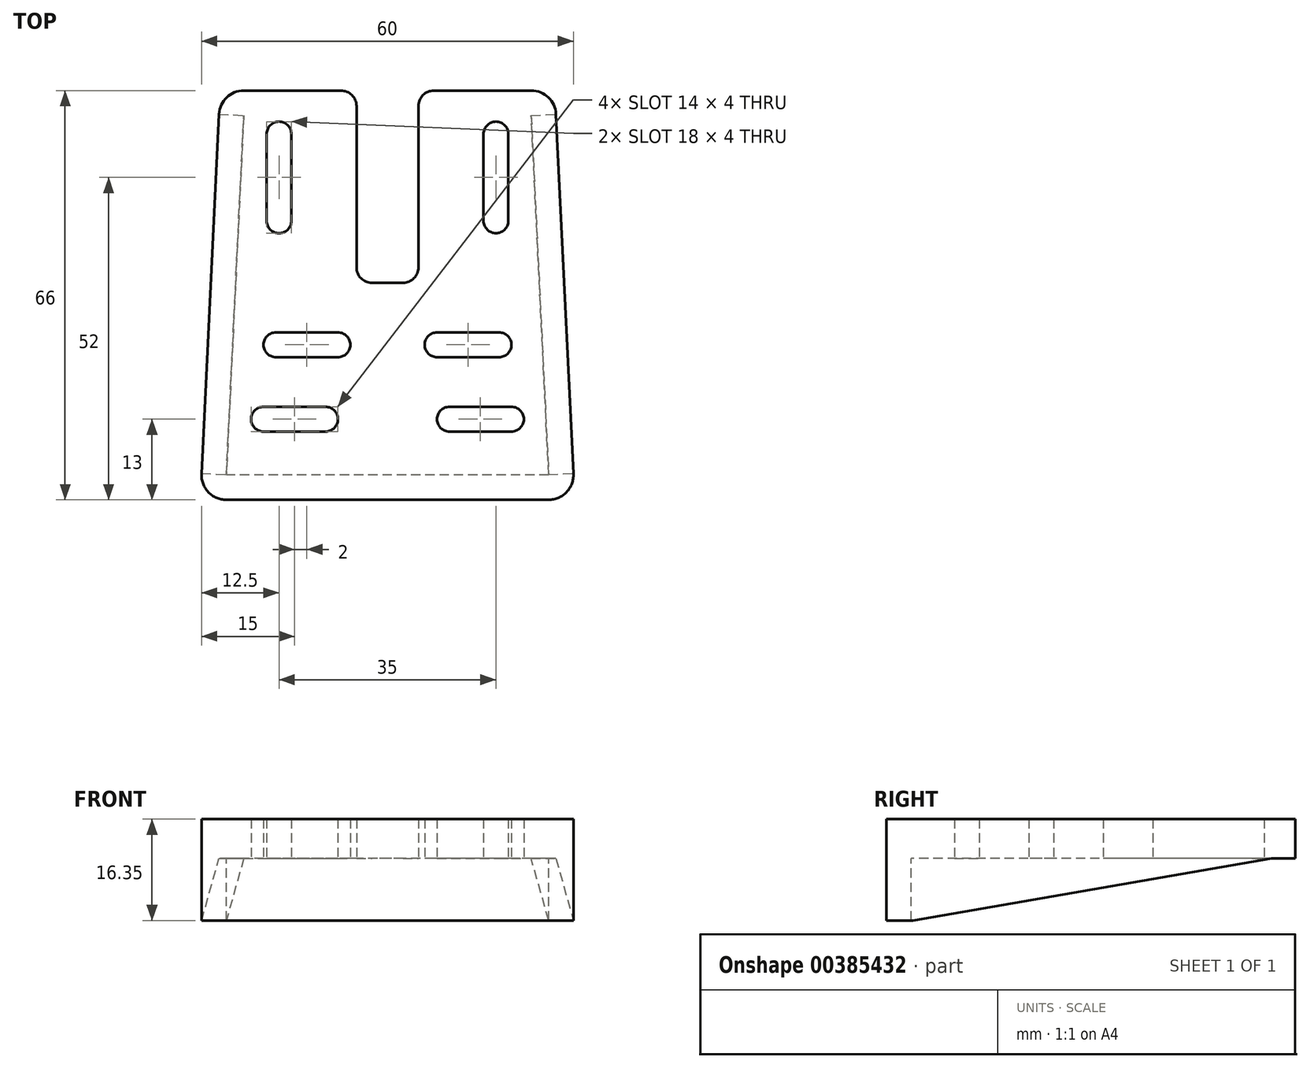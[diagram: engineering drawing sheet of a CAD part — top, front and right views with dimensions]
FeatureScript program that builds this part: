
annotation { "Feature Type Name" : "Feature", "Feature Type Description" : "" }
export const myFeature = defineFeature(function(context is Context, id is Id, definition is map)
    precondition{}
    {
        {
            var Q0;
            Q0=qCreatedBy(makeId("Top.planeOp"),FACE);
            var sketch = newSketch(context, id + "F0", { "sketchPlane" : qUnion([Q0])});
            skLineSegment(sketch, "E0", {"start": v(0, 0) * mm, "end": v(26, 0) * mm});
            skLineSegment(sketch, "E1", {"start": v(23.19, 66) * mm, "end": v(7.5, 66) * mm});
            skLineSegment(sketch, "E2", {"start": v(5, 63.5) * mm, "end": v(5, 37.5) * mm});
            skLineSegment(sketch, "E3", {"start": v(2.5, 35) * mm, "end": v(0, 35) * mm});
            skLineSegment(sketch, "E4.bottom", {"start": v(21, 61) * mm, "end": v(21, 61) * mm});
            skLineSegment(sketch, "E4.top", {"start": v(17, 35) * mm, "end": v(17, 35) * mm});
            skPoint(sketch, "E5.visualSharp", {"position": v(5, 35) * mm});
            skArc(sketch, "E5.filletArc", {"start": v(2.5, 35) * mm, "mid": v(4.27, 35.73) * mm, "end": v(5, 37.5) * mm});
            skPoint(sketch, "E6.visualSharp", {"position": v(5, 66) * mm});
            skArc(sketch, "E6.filletArc", {"start": v(7.5, 66) * mm, "mid": v(5.73, 65.27) * mm, "end": v(5, 63.5) * mm});
            skArc(sketch, "E7.filletArc", {"start": v(26, 0) * mm, "mid": v(28.9, 1.24) * mm, "end": v(30, 4.2) * mm});
            skLineSegment(sketch, "E8.MirrorCS", {"start": v(-21, 61) * mm, "end": v(-21, 61) * mm});
            skLineSegment(sketch, "E9.MirrorCS", {"start": v(-17, 35) * mm, "end": v(-17, 35) * mm});
            skLineSegment(sketch, "E10", {"start": v(17.5, 59) * mm, "end": v(17.5, 45) * mm, "construction": true});
            skArc(sketch, "E11.0.startCap", {"start": v(15.5, 59) * mm, "mid": v(17.5, 61) * mm, "end": v(19.5, 59) * mm});
            skArc(sketch, "E11.0.endCap", {"start": v(19.5, 45) * mm, "mid": v(17.5, 43) * mm, "end": v(15.5, 45) * mm});
            skLineSegment(sketch, "E11.0.left", {"start": v(19.5, 59) * mm, "end": v(19.5, 45) * mm});
            skLineSegment(sketch, "E11.0.right", {"start": v(15.5, 59) * mm, "end": v(15.5, 45) * mm});
            skLineSegment(sketch, "E12", {"start": v(27.18, 62.2) * mm, "end": v(30, 4.2) * mm});
            skPoint(sketch, "E13.visualSharp", {"position": v(27, 66) * mm});
            skArc(sketch, "E13.filletArc", {"start": v(27.18, 62.2) * mm, "mid": v(25.95, 64.9) * mm, "end": v(23.19, 66) * mm});
            skLineSegment(sketch, "E14", {"start": v(20, 13) * mm, "end": v(10, 13) * mm, "construction": true});
            skLineSegment(sketch, "E15", {"start": v(0, 35) * mm, "end": v(0, 0) * mm, "construction": true});
            skArc(sketch, "E16.0.startCap", {"start": v(20, 15) * mm, "mid": v(22, 13) * mm, "end": v(20, 11) * mm});
            skArc(sketch, "E16.0.endCap", {"start": v(10, 11) * mm, "mid": v(8, 13) * mm, "end": v(10, 15) * mm});
            skLineSegment(sketch, "E16.0.left", {"start": v(20, 11) * mm, "end": v(10, 11) * mm});
            skLineSegment(sketch, "E16.0.right", {"start": v(20, 15) * mm, "end": v(10, 15) * mm});
            skLineSegment(sketch, "E17", {"start": v(8, 25) * mm, "end": v(18, 25) * mm, "construction": true});
            skArc(sketch, "E18.0.startCap", {"start": v(8, 23) * mm, "mid": v(6, 25) * mm, "end": v(8, 27) * mm});
            skArc(sketch, "E18.0.endCap", {"start": v(18, 27) * mm, "mid": v(20, 25) * mm, "end": v(18, 23) * mm});
            skLineSegment(sketch, "E18.0.left", {"start": v(8, 27) * mm, "end": v(18, 27) * mm});
            skLineSegment(sketch, "E18.0.right", {"start": v(8, 23) * mm, "end": v(18, 23) * mm});
            skLineSegment(sketch, "E19.MirrorCS", {"start": v(0, 0) * mm, "end": v(-26, 0) * mm});
            skArc(sketch, "E20.MirrorCS", {"start": v(-26, 0) * mm, "mid": v(-28.9, 1.24) * mm, "end": v(-30, 4.2) * mm});
            skLineSegment(sketch, "E21.MirrorCS", {"start": v(-27.18, 62.2) * mm, "end": v(-30, 4.2) * mm});
            skArc(sketch, "E22.MirrorCS", {"start": v(-27.18, 62.2) * mm, "mid": v(-25.95, 64.9) * mm, "end": v(-23.19, 66) * mm});
            skLineSegment(sketch, "E23.MirrorCS", {"start": v(-23.19, 66) * mm, "end": v(-7.5, 66) * mm});
            skArc(sketch, "E24.MirrorCS", {"start": v(-7.5, 66) * mm, "mid": v(-5.73, 65.27) * mm, "end": v(-5, 63.5) * mm});
            skLineSegment(sketch, "E25.MirrorCS", {"start": v(-5, 63.5) * mm, "end": v(-5, 37.5) * mm});
            skArc(sketch, "E26.MirrorCS", {"start": v(-2.5, 35) * mm, "mid": v(-4.27, 35.73) * mm, "end": v(-5, 37.5) * mm});
            skLineSegment(sketch, "E27.MirrorCS", {"start": v(-2.5, 35) * mm, "end": v(0, 35) * mm});
            skArc(sketch, "E28.MirrorCS", {"start": v(-19.5, 45) * mm, "mid": v(-17.5, 43) * mm, "end": v(-15.5, 45) * mm});
            skLineSegment(sketch, "E29.MirrorCS", {"start": v(-15.5, 59) * mm, "end": v(-15.5, 45) * mm});
            skLineSegment(sketch, "E30.MirrorCS", {"start": v(-17.5, 59) * mm, "end": v(-17.5, 45) * mm, "construction": true});
            skArc(sketch, "E31.MirrorCS", {"start": v(-15.5, 59) * mm, "mid": v(-17.5, 61) * mm, "end": v(-19.5, 59) * mm});
            skLineSegment(sketch, "E32.MirrorCS", {"start": v(-19.5, 59) * mm, "end": v(-19.5, 45) * mm});
            skLineSegment(sketch, "E33.MirrorCS", {"start": v(-8, 27) * mm, "end": v(-18, 27) * mm});
            skArc(sketch, "E34.MirrorCS", {"start": v(-18, 27) * mm, "mid": v(-20, 25) * mm, "end": v(-18, 23) * mm});
            skLineSegment(sketch, "E35.MirrorCS", {"start": v(-8, 23) * mm, "end": v(-18, 23) * mm});
            skArc(sketch, "E36.MirrorCS", {"start": v(-8, 23) * mm, "mid": v(-6, 25) * mm, "end": v(-8, 27) * mm});
            skLineSegment(sketch, "E37.MirrorCS", {"start": v(-8, 25) * mm, "end": v(-18, 25) * mm, "construction": true});
            skLineSegment(sketch, "E38.MirrorCS", {"start": v(-20, 15) * mm, "end": v(-10, 15) * mm});
            skArc(sketch, "E39.MirrorCS", {"start": v(-10, 11) * mm, "mid": v(-8, 13) * mm, "end": v(-10, 15) * mm});
            skLineSegment(sketch, "E40.MirrorCS", {"start": v(-20, 11) * mm, "end": v(-10, 11) * mm});
            skLineSegment(sketch, "E41.MirrorCS", {"start": v(-20, 13) * mm, "end": v(-10, 13) * mm, "construction": true});
            skArc(sketch, "E42.MirrorCS", {"start": v(-20, 15) * mm, "mid": v(-22, 13) * mm, "end": v(-20, 11) * mm});
            skSolve(sketch);
        }
        {
            var Q0;
            Q0=makeQuery(id+"F0.imprint","IMPRINT",FACE,{"disambiguationData":[TD([[makeQuery(id+"F0.imprint","IMPRINT",EDGE,{"derivedFrom":sQuery(id+"F0.wireOp",EDGE,"E0")}),1.0]])]});
            extrude(context, id + "F1", {"entities" : qUnion([Q0]), "depth" : 6.35 * mm});
        }
        {
            var Q0;
            Q0=makeQuery(id+"F0.imprint","IMPRINT",FACE,{"disambiguationData":[TD([[makeQuery(id+"F0.imprint","IMPRINT",EDGE,{"derivedFrom":sQuery(id+"F0.wireOp",EDGE,"E0")}),1.0]])]});
            var sketch = newSketch(context, id + "F2", { "sketchPlane" : qUnion([Q0])});
            skLineSegment(sketch, "E43", {"start": v(30, 4.2) * mm, "end": v(27.18, 62.2) * mm});
            skLineSegment(sketch, "E44", {"start": v(23.19, 62) * mm, "end": v(26, 4) * mm});
            skLineSegment(sketch, "E45", {"start": v(26, 4) * mm, "end": v(-26, 4) * mm});
            skLineSegment(sketch, "E46", {"start": v(-26, 4) * mm, "end": v(-23.19, 62) * mm});
            skLineSegment(sketch, "E47", {"start": v(26, 0) * mm, "end": v(-26, 0) * mm});
            skLineSegment(sketch, "E48", {"start": v(-27.18, 62.2) * mm, "end": v(-30, 4.2) * mm});
            skLineSegment(sketch, "E49", {"start": v(-27.18, 62.2) * mm, "end": v(-23.19, 62) * mm});
            skLineSegment(sketch, "E50", {"start": v(-23.19, 62) * mm, "end": v(-23.19, 62) * mm});
            skLineSegment(sketch, "E51", {"start": v(23.19, 62) * mm, "end": v(27.18, 62.2) * mm});
            skArc(sketch, "E52", {"start": v(26, 0) * mm, "mid": v(28.9, 1.24) * mm, "end": v(30, 4.2) * mm});
            skArc(sketch, "E53", {"start": v(-26, 0) * mm, "mid": v(-28.9, 1.24) * mm, "end": v(-30, 4.2) * mm});
            skLineSegment(sketch, "E54", {"start": v(-30, 4.2) * mm, "end": v(-26, 4) * mm});
            skLineSegment(sketch, "E55", {"start": v(26, 4) * mm, "end": v(30, 4.2) * mm});
            skSolve(sketch);
        }
        {
            var Q0;
            Q0=makeQuery(id+"F2.imprint","IMPRINT",FACE,{"disambiguationData":[TD([[makeQuery(id+"F2.imprint","IMPRINT",EDGE,{"derivedFrom":sQuery(id+"F2.wireOp",EDGE,"E45")}),1.0]])]});
            var Q1;
            Q1=makeQuery(id+"F2.imprint","IMPRINT",FACE,{"disambiguationData":[TD([[makeQuery(id+"F2.imprint","IMPRINT",EDGE,{"derivedFrom":sQuery(id+"F2.wireOp",EDGE,"E46")}),1.0]])]});
            var Q2;
            Q2=makeQuery(id+"F2.imprint","IMPRINT",FACE,{"disambiguationData":[TD([[makeQuery(id+"F2.imprint","IMPRINT",EDGE,{"derivedFrom":sQuery(id+"F2.wireOp",EDGE,"E43")}),-1.0]])]});
            extrude(context, id + "F3", {"entities" : qUnion([Q0, Q1, Q2]), "operationType" : NewBodyOperationType.ADD, "oppositeDirection" : true, "depth" : 10 * mm});
        }
        {
            var Q0;
            Q0=makeQuery(id+"F3.opExtrude","CAP_EDGE",EDGE,{"disambiguationData":[OSD([sQuery(id+"F2.wireOp",EDGE,"E49")])],"isStart":false});
            chamfer(context, id + "F4", {"entities" : qUnion([Q0]), "chamferType" : ChamferType.TWO_OFFSETS, "width1" : 58 * mm, "oppositeDirection" : false, "width2" : 10 * mm, "tangentPropagation" : true});
        }
        {
            var Q0;
            Q0=makeQuery(id+"F3.opExtrude","CAP_EDGE",EDGE,{"disambiguationData":[OSD([sQuery(id+"F2.wireOp",EDGE,"E51")])],"isStart":false});
            chamfer(context, id + "F5", {"entities" : qUnion([Q0]), "chamferType" : ChamferType.TWO_OFFSETS, "width1" : 58 * mm, "oppositeDirection" : false, "width2" : 10 * mm, "tangentPropagation" : true});
        }
    });
